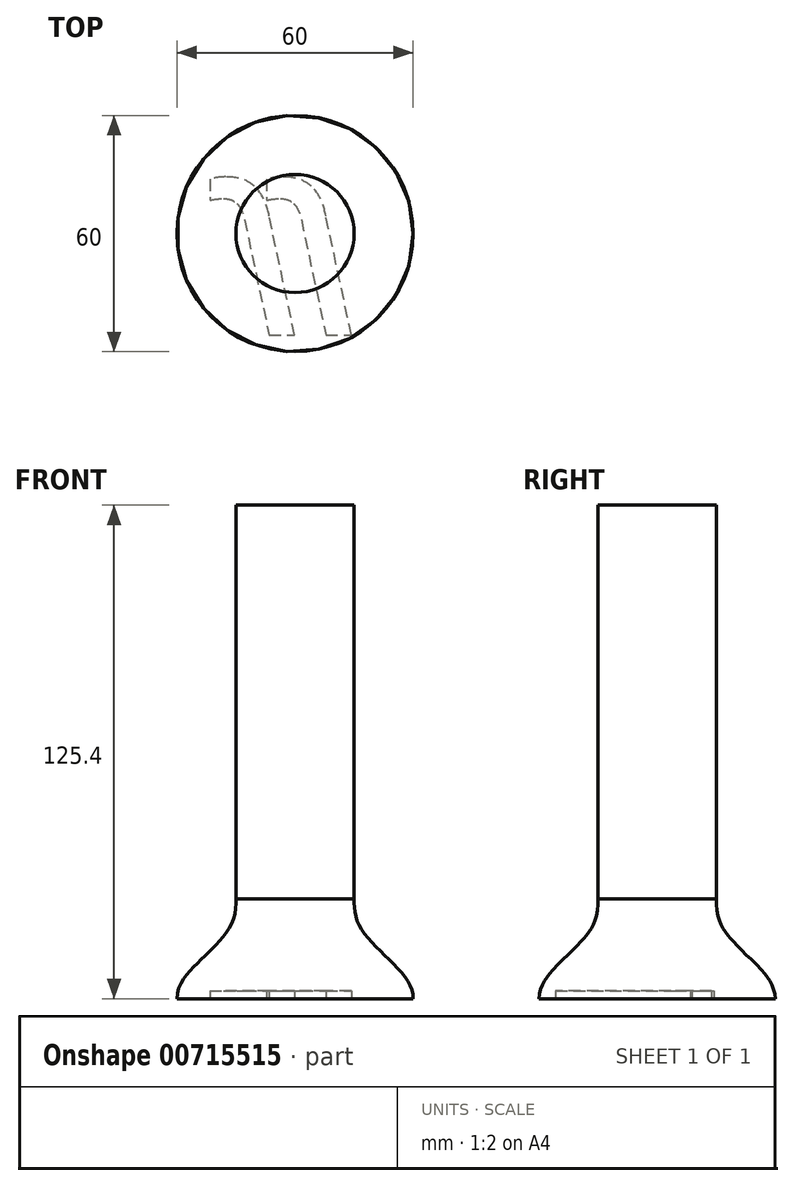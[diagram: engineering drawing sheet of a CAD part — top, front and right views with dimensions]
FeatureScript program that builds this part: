
annotation { "Feature Type Name" : "Feature", "Feature Type Description" : "" }
export const myFeature = defineFeature(function(context is Context, id is Id, definition is map)
    precondition{}
    {
        {
            var Q0;
            Q0=qCreatedBy(makeId("Top.planeOp"),FACE);
            var sketch = newSketch(context, id + "F0", { "sketchPlane" : qUnion([Q0])});
            skCircle(sketch, "E0", {"center": v(0, 0) * mm, "radius": 15 * mm});
            skSolve(sketch);
        }
        {
            var Q0;
            Q0=qSketchRegion(id+"F0",true);
            var Q1;
            Q1=sQuery(id+"F0.wireOp",EDGE,"E0");
            extrude(context, id + "F1", {"entities" : qUnion([Q0]), "surfaceEntities" : qUnion([Q1]), "depth" : 100 * mm, "offsetDistance" : 25.4 * mm});
        }
        {
            var Q0;
            Q0=qCreatedBy(makeId("Top.planeOp"),FACE);
            cPlane(context, id + "F2", {"entities" : qUnion([Q0]), "cplaneType" : CPlaneType.OFFSET, "offset" : 25.4 * mm, "oppositeDirection" : true, "width" : 152.4 * mm, "height" : 152.4 * mm});
        }
        {
            var Q0;
            Q0=qCreatedBy(id+"F2.planeOp",FACE);
            var sketch = newSketch(context, id + "F3", { "sketchPlane" : qUnion([Q0])});
            skCircle(sketch, "E1", {"center": v(0, 0) * mm, "radius": 30 * mm});
            skSolve(sketch);
        }
        {
            var Q0;
            Q0=makeQuery(id+"F3.imprint","IMPRINT",FACE,{"disambiguationData":[TD([[makeQuery(id+"F3.imprint","IMPRINT",EDGE,{"derivedFrom":sQuery(id+"F3.wireOp",EDGE,"E1")}),1.0]])]});
            var Q1;
            Q1=makeQuery(id+"F1.opExtrude","CAP_FACE",FACE,{"disambiguationData":[OSD([sQuery(id+"F0.wireOp",EDGE,"E0")])],"isStart":true});
            loft(context, id + "F4", {"startCondition" : LoftEndDerivativeType.NORMAL_TO_PROFILE, "startMagnitude" : 1, "endCondition" : LoftEndDerivativeType.MATCH_CURVATURE, "endMagnitude" : 1, "sheetProfilesArray" : [{ "sheetProfileEntities" : qUnion([Q0]) }, { "sheetProfileEntities" : qUnion([Q1]) }]});
        }
        {
            var Q0;
            Q0=makeQuery(id+"F4.opLoft","CAP_FACE",FACE,{"disambiguationData":[OSD([makeQuery(id+"F3.imprint","IMPRINT",FACE,{"disambiguationData":[TD([[makeQuery(id+"F3.imprint","IMPRINT",EDGE,{"derivedFrom":sQuery(id+"F3.wireOp",EDGE,"E1")}),1.0]])]})])],"isStart":true});
            var sketch = newSketch(context, id + "F5", { "sketchPlane" : qUnion([Q0])});
            skText(sketch, "E2", { "text": "JJ", "fontName": "OpenSans-BoldItalic.ttf"});
            const initialGuessF5  = {"E2": [-0.01479, -0.00526, 1, 0, 0.03136]};
            skSetInitialGuess(sketch, initialGuessF5);
            skSolve(sketch);
        }
        {
            var Q0;
            Q0=qSketchRegion(id+"F5",true);
            extrude(context, id + "F6", {"entities" : qUnion([Q0]), "oppositeDirection" : true, "depth" : 2 * mm, "offsetDistance" : 25.4 * mm});
        }
        {
            var Q0;
            Q0=makeQuery(id+"F6.opExtrude","SWEPT_BODY",BODY,{"disambiguationData":[OSD([sQuery(id+"F5.wireOp",EDGE,"E2.sketch_text.stroke-0"),sQuery(id+"F5.wireOp",EDGE,"E2.sketch_text.stroke-1"),sQuery(id+"F5.wireOp",EDGE,"E2.sketch_text.stroke-2"),sQuery(id+"F5.wireOp",EDGE,"E2.sketch_text.stroke-3"),sQuery(id+"F5.wireOp",EDGE,"E2.sketch_text.stroke-4"),sQuery(id+"F5.wireOp",EDGE,"E2.sketch_text.stroke-5"),sQuery(id+"F5.wireOp",EDGE,"E2.sketch_text.stroke-6"),sQuery(id+"F5.wireOp",EDGE,"E2.sketch_text.stroke-7"),sQuery(id+"F5.wireOp",EDGE,"E2.sketch_text.stroke-8"),sQuery(id+"F5.wireOp",EDGE,"E2.sketch_text.stroke-9")])]});
            var Q1;
            Q1=makeQuery(id+"F6.opExtrude","SWEPT_BODY",BODY,{"disambiguationData":[OSD([sQuery(id+"F5.wireOp",EDGE,"E2.sketch_text.stroke-10"),sQuery(id+"F5.wireOp",EDGE,"E2.sketch_text.stroke-11"),sQuery(id+"F5.wireOp",EDGE,"E2.sketch_text.stroke-12"),sQuery(id+"F5.wireOp",EDGE,"E2.sketch_text.stroke-13"),sQuery(id+"F5.wireOp",EDGE,"E2.sketch_text.stroke-14"),sQuery(id+"F5.wireOp",EDGE,"E2.sketch_text.stroke-15"),sQuery(id+"F5.wireOp",EDGE,"E2.sketch_text.stroke-16"),sQuery(id+"F5.wireOp",EDGE,"E2.sketch_text.stroke-17"),sQuery(id+"F5.wireOp",EDGE,"E2.sketch_text.stroke-18"),sQuery(id+"F5.wireOp",EDGE,"E2.sketch_text.stroke-19")])]});
            var Q2;
            Q2=makeQuery(id+"F4.opLoft","SWEPT_BODY",BODY,{"disambiguationData":[OSD([sQuery(id+"F0.wireOp",EDGE,"E0"),makeQuery(id+"F3.imprint","IMPRINT",FACE,{"disambiguationData":[TD([[makeQuery(id+"F3.imprint","IMPRINT",EDGE,{"derivedFrom":sQuery(id+"F3.wireOp",EDGE,"E1")}),1.0]])]})])]});
            booleanBodies(context, id + "F7", {"operationType" : BooleanOperationType.SUBTRACTION, "tools" : qUnion([Q0, Q1]), "targets" : qUnion([Q2])});
        }
    });
